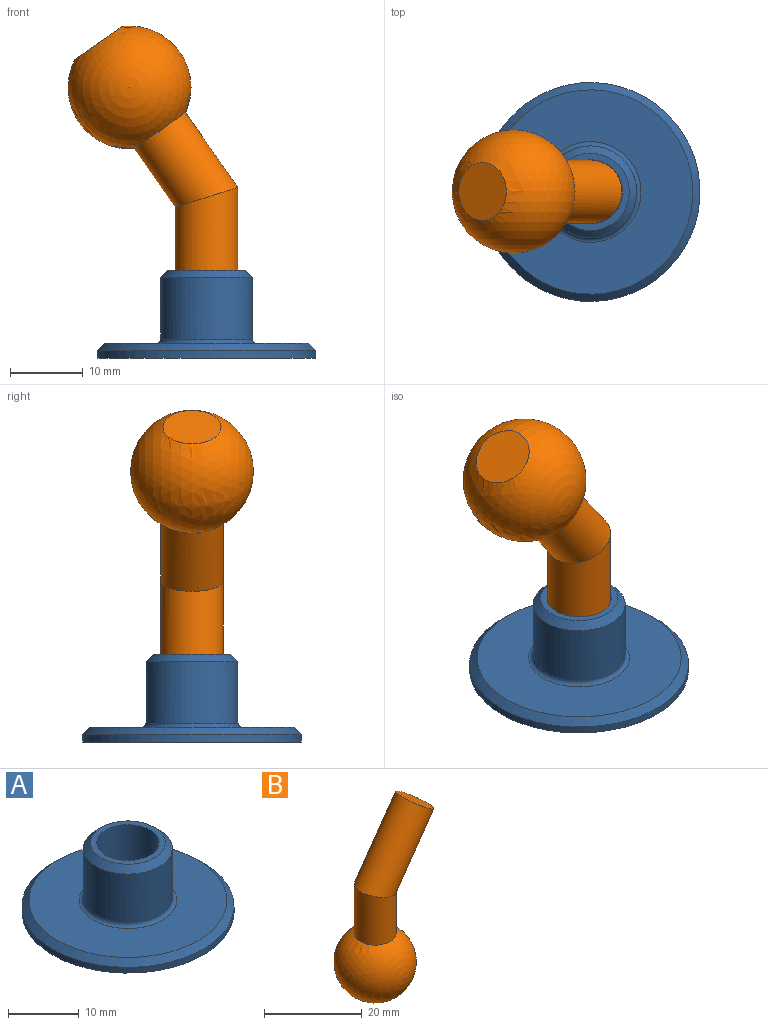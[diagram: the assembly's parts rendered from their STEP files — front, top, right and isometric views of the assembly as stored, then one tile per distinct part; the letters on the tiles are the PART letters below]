
ASSEMBLY  parts=2 mates=1
PART A: 11 faces, bbox 30x30x12 mm
  f0: cylinder r=6.3mm len=12.6mm, axis (0,0,-1), area 332.5mm2, adj f8,f10
  f1: plane 10.6x10.6mm, normal (0,0,1), area 27.4mm2, adj f2,f8
  f2: cylinder r=4.4mm len=10mm, axis (0,0,-1), area 276.5mm2, adj f1,f3
  f3: plane 8.8x8.8mm, normal (0,0,1), area 53.8mm2, adj f2,f5
  f4: cylinder r=15mm len=30mm, axis (0,0,1), area 94.2mm2, adj f6,f9
  f5: cylinder r=1.5mm len=3mm, axis (0,0,1), area 18.8mm2, adj f3,f6
  f6: plane 30x30mm, normal (0,0,-1), area 699.8mm2, adj f4,f5
  f7: plane 28x28mm, normal (0,0,1), area 466.2mm2, adj f9,f10
  f8: cone r=5.3mm half-angle=45deg, axis (0,0,-1), area 51.5mm2, adj f0,f1
  f9: cone r=15mm half-angle=45deg, axis (0,0,-1), area 128.8mm2, adj f4,f7
  f10: torus R=6.9mm, axis (0,0,-1), area 38.6mm2, adj f0,f7
PART B: 5 faces, bbox 23.4x16.8x45.7 mm
  f0: sphere r=8.42mm, area 775.5mm2, adj f3,f4
  f1: plane 8.6x7.04mm, normal (0.57,0,0.82), area 58.1mm2, adj f2
  f2: cylinder r=4.3mm len=22.43mm, axis (0.57,0,0.82), area 540.4mm2, adj f1,f3
  f3: cylinder r=4.3mm len=12.52mm, axis (0,0,1), area 301.5mm2, adj f0,f2
  f4: plane 7.96x7.96mm, normal (0,0,-1), area 49.8mm2, adj f0
PLACE A t=(17.3,12.65,3.3)mm
PLACE B rot(axis=(0,1,0),145deg) t=(6.75,12.65,38.38)mm
MATE fastened A.f5 <-> B.f2  axis (0,0,1) through (17.3,12.65,3.3)mm
